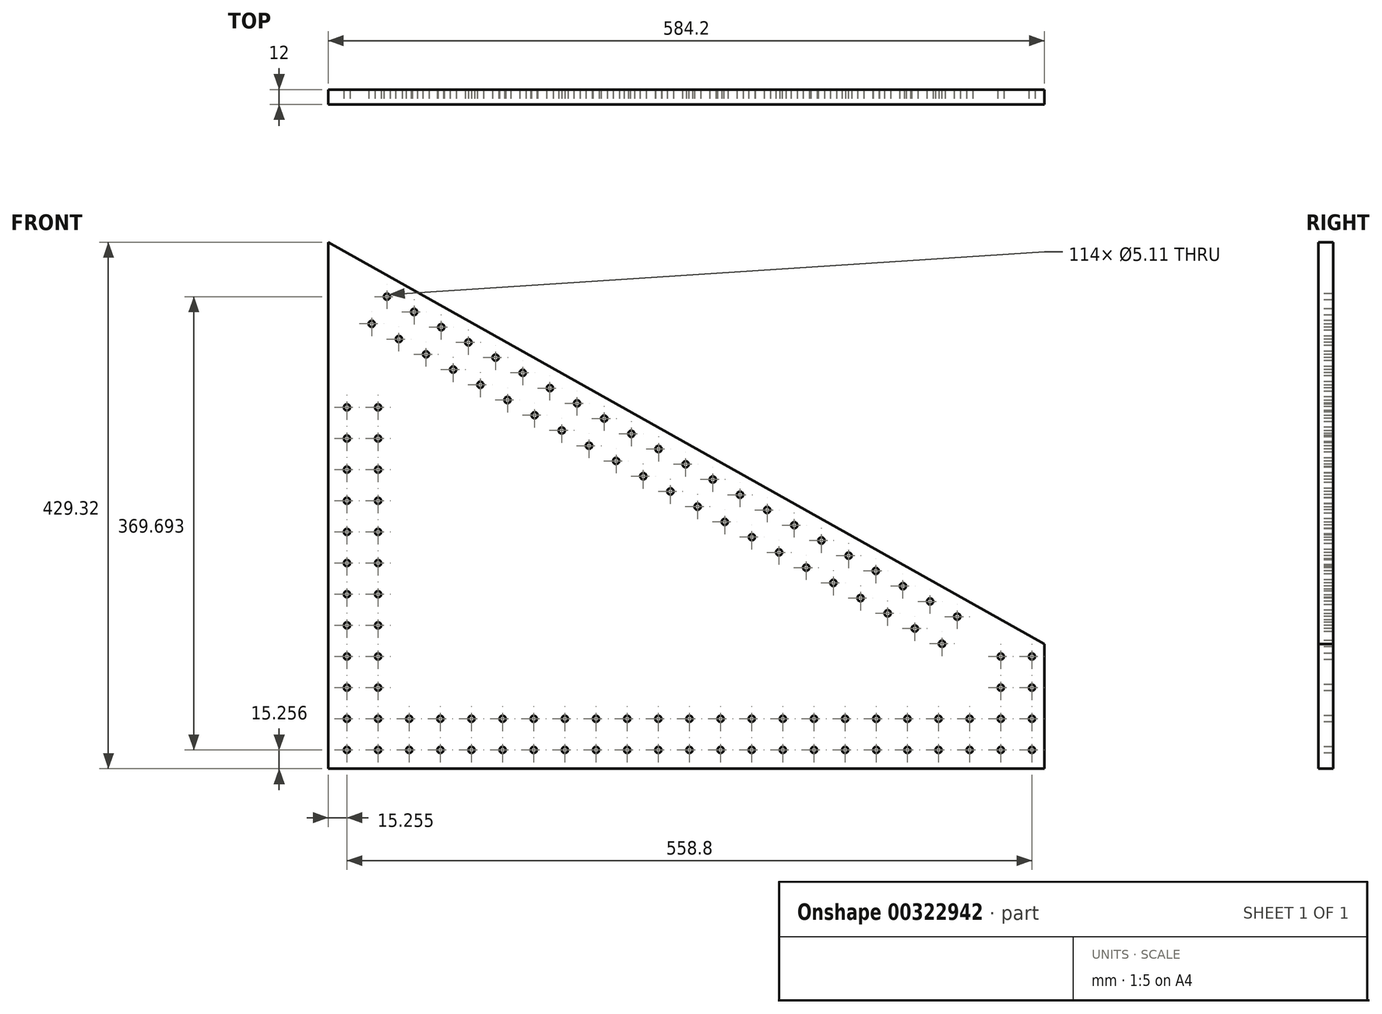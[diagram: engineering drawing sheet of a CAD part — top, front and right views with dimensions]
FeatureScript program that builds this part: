
annotation { "Feature Type Name" : "Feature", "Feature Type Description" : "" }
export const myFeature = defineFeature(function(context is Context, id is Id, definition is map)
    precondition{}
    {
        {
            var Q0;
            Q0=qCreatedBy(makeId("Front.planeOp"),FACE);
            var sketch = newSketch(context, id + "F0", { "sketchPlane" : qUnion([Q0])});
            skLineSegment(sketch, "E0", {"start": v(-72.97, 69.02) * mm, "end": v(-72.97, -360.3) * mm});
            skLineSegment(sketch, "E1", {"start": v(511.23, -258.7) * mm, "end": v(511.23, -360.3) * mm});
            skLineSegment(sketch, "E2", {"start": v(511.23, -258.7) * mm, "end": v(-72.97, 69.02) * mm});
            skLineSegment(sketch, "E3", {"start": v(-72.97, -360.3) * mm, "end": v(511.23, -360.3) * mm});
            skSolve(sketch);
        }
        {
            var Q0;
            Q0=makeQuery(id+"F0.imprint","IMPRINT",FACE,{"disambiguationData":[TD([[makeQuery(id+"F0.imprint","IMPRINT",EDGE,{"derivedFrom":sQuery(id+"F0.wireOp",EDGE,"E0")}),1.0]])]});
            extrude(context, id + "F1", {"entities" : qUnion([Q0]), "depth" : 12 * mm});
        }
        {
            var Q0;
            Q0=makeQuery(id+"F1.opExtrude","CAP_FACE",FACE,{"disambiguationData":[OSD([sQuery(id+"F0.wireOp",EDGE,"E0"),sQuery(id+"F0.wireOp",EDGE,"E1"),sQuery(id+"F0.wireOp",EDGE,"E2"),sQuery(id+"F0.wireOp",EDGE,"E3")])],"isStart":false});
            var sketch = newSketch(context, id + "F2", { "sketchPlane" : qUnion([Q0])});
            skCircle(sketch, "E4", {"center": v(-57.71, -345.04) * mm, "radius": 2.55 * mm});
            skCircle(sketch, "E5.0.1.0", {"center": v(-57.71, -319.64) * mm, "radius": 2.55 * mm});
            skCircle(sketch, "E5.0.2.0", {"center": v(-57.71, -294.24) * mm, "radius": 2.55 * mm});
            skCircle(sketch, "E5.0.3.0", {"center": v(-57.71, -268.84) * mm, "radius": 2.55 * mm});
            skCircle(sketch, "E5.0.4.0", {"center": v(-57.71, -243.44) * mm, "radius": 2.55 * mm});
            skCircle(sketch, "E5.0.5.0", {"center": v(-57.71, -218.04) * mm, "radius": 2.55 * mm});
            skCircle(sketch, "E5.0.6.0", {"center": v(-57.71, -192.64) * mm, "radius": 2.55 * mm});
            skCircle(sketch, "E5.0.7.0", {"center": v(-57.71, -167.24) * mm, "radius": 2.55 * mm});
            skCircle(sketch, "E5.0.8.0", {"center": v(-57.71, -141.84) * mm, "radius": 2.55 * mm});
            skCircle(sketch, "E5.0.9.0", {"center": v(-57.71, -116.44) * mm, "radius": 2.55 * mm});
            skCircle(sketch, "E5.0.10.0", {"center": v(-57.71, -91.04) * mm, "radius": 2.55 * mm});
            skCircle(sketch, "E5.0.11.0", {"center": v(-57.71, -65.64) * mm, "radius": 2.55 * mm});
            skCircle(sketch, "E5.1.0.0", {"center": v(-32.31, -345.04) * mm, "radius": 2.55 * mm});
            skCircle(sketch, "E5.1.1.0", {"center": v(-32.31, -319.64) * mm, "radius": 2.55 * mm});
            skCircle(sketch, "E5.1.2.0", {"center": v(-32.31, -294.24) * mm, "radius": 2.55 * mm});
            skCircle(sketch, "E5.1.3.0", {"center": v(-32.31, -268.84) * mm, "radius": 2.55 * mm});
            skCircle(sketch, "E5.1.4.0", {"center": v(-32.31, -243.44) * mm, "radius": 2.55 * mm});
            skCircle(sketch, "E5.1.5.0", {"center": v(-32.31, -218.04) * mm, "radius": 2.55 * mm});
            skCircle(sketch, "E5.1.6.0", {"center": v(-32.31, -192.64) * mm, "radius": 2.55 * mm});
            skCircle(sketch, "E5.1.7.0", {"center": v(-32.31, -167.24) * mm, "radius": 2.55 * mm});
            skCircle(sketch, "E5.1.8.0", {"center": v(-32.31, -141.84) * mm, "radius": 2.55 * mm});
            skCircle(sketch, "E5.1.9.0", {"center": v(-32.31, -116.44) * mm, "radius": 2.55 * mm});
            skCircle(sketch, "E5.1.10.0", {"center": v(-32.31, -91.04) * mm, "radius": 2.55 * mm});
            skCircle(sketch, "E5.1.11.0", {"center": v(-32.31, -65.64) * mm, "radius": 2.55 * mm});
            skLineSegment(sketch, "E5.direction1", {"start": v(-57.71, -345.04) * mm, "end": v(-32.31, -345.04) * mm, "construction": true});
            skLineSegment(sketch, "E5.direction2", {"start": v(-57.71, -345.04) * mm, "end": v(-57.71, -319.64) * mm, "construction": true});
            skCircle(sketch, "E6.1.0.0", {"center": v(-6.91, -319.64) * mm, "radius": 2.55 * mm});
            skCircle(sketch, "E6.1.0.1", {"center": v(-6.91, -345.04) * mm, "radius": 2.55 * mm});
            skCircle(sketch, "E6.2.0.0", {"center": v(18.49, -319.64) * mm, "radius": 2.55 * mm});
            skCircle(sketch, "E6.2.0.1", {"center": v(18.49, -345.04) * mm, "radius": 2.55 * mm});
            skCircle(sketch, "E6.3.0.0", {"center": v(43.89, -319.64) * mm, "radius": 2.55 * mm});
            skCircle(sketch, "E6.3.0.1", {"center": v(43.89, -345.04) * mm, "radius": 2.55 * mm});
            skCircle(sketch, "E6.4.0.0", {"center": v(69.29, -319.64) * mm, "radius": 2.55 * mm});
            skCircle(sketch, "E6.4.0.1", {"center": v(69.29, -345.04) * mm, "radius": 2.55 * mm});
            skCircle(sketch, "E6.5.0.0", {"center": v(94.69, -319.64) * mm, "radius": 2.55 * mm});
            skCircle(sketch, "E6.5.0.1", {"center": v(94.69, -345.04) * mm, "radius": 2.55 * mm});
            skCircle(sketch, "E6.6.0.0", {"center": v(120.09, -319.64) * mm, "radius": 2.55 * mm});
            skCircle(sketch, "E6.6.0.1", {"center": v(120.09, -345.04) * mm, "radius": 2.55 * mm});
            skCircle(sketch, "E6.7.0.0", {"center": v(145.49, -319.64) * mm, "radius": 2.55 * mm});
            skCircle(sketch, "E6.7.0.1", {"center": v(145.49, -345.04) * mm, "radius": 2.55 * mm});
            skCircle(sketch, "E6.8.0.0", {"center": v(170.89, -319.64) * mm, "radius": 2.55 * mm});
            skCircle(sketch, "E6.8.0.1", {"center": v(170.89, -345.04) * mm, "radius": 2.55 * mm});
            skCircle(sketch, "E6.9.0.0", {"center": v(196.29, -319.64) * mm, "radius": 2.55 * mm});
            skCircle(sketch, "E6.9.0.1", {"center": v(196.29, -345.04) * mm, "radius": 2.55 * mm});
            skCircle(sketch, "E6.10.0.0", {"center": v(221.69, -319.64) * mm, "radius": 2.55 * mm});
            skCircle(sketch, "E6.10.0.1", {"center": v(221.69, -345.04) * mm, "radius": 2.55 * mm});
            skCircle(sketch, "E6.11.0.0", {"center": v(247.09, -319.64) * mm, "radius": 2.55 * mm});
            skCircle(sketch, "E6.11.0.1", {"center": v(247.09, -345.04) * mm, "radius": 2.55 * mm});
            skCircle(sketch, "E6.12.0.0", {"center": v(272.49, -319.64) * mm, "radius": 2.55 * mm});
            skCircle(sketch, "E6.12.0.1", {"center": v(272.49, -345.04) * mm, "radius": 2.55 * mm});
            skCircle(sketch, "E6.13.0.0", {"center": v(297.89, -319.64) * mm, "radius": 2.55 * mm});
            skCircle(sketch, "E6.13.0.1", {"center": v(297.89, -345.04) * mm, "radius": 2.55 * mm});
            skCircle(sketch, "E6.14.0.0", {"center": v(323.29, -319.64) * mm, "radius": 2.55 * mm});
            skCircle(sketch, "E6.14.0.1", {"center": v(323.29, -345.04) * mm, "radius": 2.55 * mm});
            skCircle(sketch, "E6.15.0.0", {"center": v(348.69, -319.64) * mm, "radius": 2.55 * mm});
            skCircle(sketch, "E6.15.0.1", {"center": v(348.69, -345.04) * mm, "radius": 2.55 * mm});
            skCircle(sketch, "E6.16.0.0", {"center": v(374.09, -319.64) * mm, "radius": 2.55 * mm});
            skCircle(sketch, "E6.16.0.1", {"center": v(374.09, -345.04) * mm, "radius": 2.55 * mm});
            skCircle(sketch, "E6.17.0.0", {"center": v(399.49, -319.64) * mm, "radius": 2.55 * mm});
            skCircle(sketch, "E6.17.0.1", {"center": v(399.49, -345.04) * mm, "radius": 2.55 * mm});
            skCircle(sketch, "E6.18.0.0", {"center": v(424.89, -319.64) * mm, "radius": 2.55 * mm});
            skCircle(sketch, "E6.18.0.1", {"center": v(424.89, -345.04) * mm, "radius": 2.55 * mm});
            skCircle(sketch, "E6.19.0.0", {"center": v(450.29, -319.64) * mm, "radius": 2.55 * mm});
            skCircle(sketch, "E6.19.0.1", {"center": v(450.29, -345.04) * mm, "radius": 2.55 * mm});
            skCircle(sketch, "E6.20.0.0", {"center": v(475.69, -319.64) * mm, "radius": 2.55 * mm});
            skCircle(sketch, "E6.20.0.1", {"center": v(475.69, -345.04) * mm, "radius": 2.55 * mm});
            skLineSegment(sketch, "E6.direction1", {"start": v(-32.31, -319.64) * mm, "end": v(-6.91, -319.64) * mm, "construction": true});
            skLineSegment(sketch, "E7", {"start": v(-28.66, 44.17) * mm, "end": v(-60.9, -13.32) * mm, "construction": true});
            skCircle(sketch, "E8", {"center": v(-25.05, 24.65) * mm, "radius": 2.55 * mm});
            skCircle(sketch, "E9.0.0.17", {"center": v(-57.71, 86.76) * mm, "radius": 2.55 * mm});
            skCircle(sketch, "E9.0.1.17", {"center": v(-32.31, 86.76) * mm, "radius": 2.55 * mm});
            skCircle(sketch, "E10.0.21.0", {"center": v(501.09, -319.64) * mm, "radius": 2.55 * mm});
            skCircle(sketch, "E10.2.21.0", {"center": v(501.09, -345.04) * mm, "radius": 2.55 * mm});
            skCircle(sketch, "E11.0.1.0", {"center": v(-37.48, 2.5) * mm, "radius": 2.55 * mm});
            skCircle(sketch, "E11.1.0.0", {"center": v(-2.9, 12.22) * mm, "radius": 2.55 * mm});
            skCircle(sketch, "E11.1.1.0", {"center": v(-15.32, -9.93) * mm, "radius": 2.55 * mm});
            skCircle(sketch, "E11.2.0.0", {"center": v(19.26, -0.2) * mm, "radius": 2.55 * mm});
            skCircle(sketch, "E11.2.1.0", {"center": v(6.83, -22.36) * mm, "radius": 2.55 * mm});
            skCircle(sketch, "E11.3.0.0", {"center": v(41.4, -12.63) * mm, "radius": 2.55 * mm});
            skCircle(sketch, "E11.3.1.0", {"center": v(28.98, -34.78) * mm, "radius": 2.55 * mm});
            skCircle(sketch, "E11.4.0.0", {"center": v(63.56, -25.06) * mm, "radius": 2.55 * mm});
            skCircle(sketch, "E11.4.1.0", {"center": v(51.13, -47.21) * mm, "radius": 2.55 * mm});
            skCircle(sketch, "E11.5.0.0", {"center": v(85.71, -37.48) * mm, "radius": 2.55 * mm});
            skCircle(sketch, "E11.5.1.0", {"center": v(73.29, -59.64) * mm, "radius": 2.55 * mm});
            skCircle(sketch, "E11.6.0.0", {"center": v(107.87, -49.91) * mm, "radius": 2.55 * mm});
            skCircle(sketch, "E11.6.1.0", {"center": v(95.44, -72.06) * mm, "radius": 2.55 * mm});
            skCircle(sketch, "E11.7.0.0", {"center": v(130.02, -62.34) * mm, "radius": 2.55 * mm});
            skCircle(sketch, "E11.7.1.0", {"center": v(117.6, -84.5) * mm, "radius": 2.55 * mm});
            skCircle(sketch, "E11.8.0.0", {"center": v(152.17, -74.77) * mm, "radius": 2.55 * mm});
            skCircle(sketch, "E11.8.1.0", {"center": v(139.75, -96.92) * mm, "radius": 2.55 * mm});
            skCircle(sketch, "E11.9.0.0", {"center": v(174.32, -87.2) * mm, "radius": 2.55 * mm});
            skCircle(sketch, "E11.9.1.0", {"center": v(161.9, -109.34) * mm, "radius": 2.55 * mm});
            skCircle(sketch, "E11.10.0.0", {"center": v(196.48, -99.62) * mm, "radius": 2.55 * mm});
            skCircle(sketch, "E11.10.1.0", {"center": v(184.05, -121.77) * mm, "radius": 2.55 * mm});
            skCircle(sketch, "E11.11.0.0", {"center": v(218.63, -112.05) * mm, "radius": 2.55 * mm});
            skCircle(sketch, "E11.11.1.0", {"center": v(206.2, -134.2) * mm, "radius": 2.55 * mm});
            skCircle(sketch, "E11.12.0.0", {"center": v(240.78, -124.47) * mm, "radius": 2.55 * mm});
            skCircle(sketch, "E11.12.1.0", {"center": v(228.36, -146.62) * mm, "radius": 2.55 * mm});
            skCircle(sketch, "E11.13.0.0", {"center": v(262.93, -136.9) * mm, "radius": 2.55 * mm});
            skCircle(sketch, "E11.13.1.0", {"center": v(250.5, -159.05) * mm, "radius": 2.55 * mm});
            skCircle(sketch, "E11.14.0.0", {"center": v(285.09, -149.33) * mm, "radius": 2.55 * mm});
            skCircle(sketch, "E11.14.1.0", {"center": v(272.66, -171.48) * mm, "radius": 2.55 * mm});
            skCircle(sketch, "E11.15.0.0", {"center": v(307.24, -161.75) * mm, "radius": 2.55 * mm});
            skCircle(sketch, "E11.15.1.0", {"center": v(294.81, -183.9) * mm, "radius": 2.55 * mm});
            skCircle(sketch, "E11.16.0.0", {"center": v(329.4, -174.18) * mm, "radius": 2.55 * mm});
            skCircle(sketch, "E11.16.1.0", {"center": v(316.97, -196.33) * mm, "radius": 2.55 * mm});
            skCircle(sketch, "E11.17.0.0", {"center": v(351.54, -186.6) * mm, "radius": 2.55 * mm});
            skCircle(sketch, "E11.17.1.0", {"center": v(339.12, -208.76) * mm, "radius": 2.55 * mm});
            skCircle(sketch, "E11.18.0.0", {"center": v(373.7, -199.03) * mm, "radius": 2.55 * mm});
            skCircle(sketch, "E11.18.1.0", {"center": v(361.27, -221.19) * mm, "radius": 2.55 * mm});
            skCircle(sketch, "E11.19.0.0", {"center": v(395.85, -211.46) * mm, "radius": 2.55 * mm});
            skCircle(sketch, "E11.19.1.0", {"center": v(383.42, -233.61) * mm, "radius": 2.55 * mm});
            skCircle(sketch, "E11.20.0.0", {"center": v(418, -223.89) * mm, "radius": 2.55 * mm});
            skCircle(sketch, "E11.20.1.0", {"center": v(405.58, -246.04) * mm, "radius": 2.55 * mm});
            skCircle(sketch, "E11.21.0.0", {"center": v(440.15, -236.31) * mm, "radius": 2.55 * mm});
            skCircle(sketch, "E11.21.1.0", {"center": v(427.73, -258.47) * mm, "radius": 2.55 * mm});
            skLineSegment(sketch, "E11.direction1", {"start": v(-25.05, 24.65) * mm, "end": v(-2.9, 12.22) * mm, "construction": true});
            skLineSegment(sketch, "E11.direction2", {"start": v(-25.05, 24.65) * mm, "end": v(-37.48, 2.5) * mm, "construction": true});
            skCircle(sketch, "E12", {"center": v(475.69, -294.24) * mm, "radius": 2.55 * mm});
            skCircle(sketch, "E13", {"center": v(475.69, -268.84) * mm, "radius": 2.55 * mm});
            skCircle(sketch, "E14", {"center": v(501.09, -294.24) * mm, "radius": 2.55 * mm});
            skCircle(sketch, "E15", {"center": v(501.09, -268.84) * mm, "radius": 2.55 * mm});
            skSolve(sketch);
        }
        {
            var Q0;
            Q0 = qSketchRegion(id + "F2", true);
            extrude(context, id + "F3", {"entities" : qUnion([Q0]), "operationType" : NewBodyOperationType.REMOVE, "oppositeDirection" : true, "depth" : 508 * mm});
        }
    });
